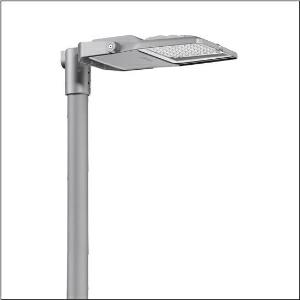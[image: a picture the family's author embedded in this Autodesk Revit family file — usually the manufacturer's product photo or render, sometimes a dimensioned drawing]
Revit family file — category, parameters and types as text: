
# Revit family: floodlight_fl_21_mini___pl33t_5xa7775c2f3a_8bfe
name_source: partatom
category: Lighting Fixtures
units: mm (PartAtom-declared; Revit-internal decimal feet)

## family parameters
Cut with Voids When Loaded = No
Host = Face
Light Source = No
Part Type = Normal
Room Calculation Point = No
Round Connector Dimension = Use Diameter
Shared = No

## types (1)
- --- (1 x LED, 12050 lm, 89 W, 3000K)
    Apparent Load = 89 VA
    CIE Flux Codes = 26 75 99 100 100
    Color Rendering = 70
    Color Temperature = 3000K
    Default Elevation = 1800 mm
    Description = Floodlight FL 21 mini, floodlight, primary light control with lens, of PMMA, primary optical cover: protective disc, of toughened safety glass, transparent, light distribution: PL33T, light emission: direct distribution, installation type: surface-mounted, LED, High Power LED, rated luminous flux: 12.050lm, luminous efficacy: 135lm/W, light colour: 730, colour temperature: 3000K, control: flexible luminous flux parameterisation, time-dependent luminous flux control, constant luminous flux control, overheat protection, presetting dimming logarithmic, with terminal, 6-pole, mains connection: 220..240V, AC, 50/60Hz, start of lifetime: 89W, end of service life: 94W, reduction: 43W, luminaire housing, of diecast aluminium, powder-coated, Siteco® metallic grey (DB 702S), corrosivity category C5 mid according to DIN EN ISO 12944, sealing non-destructively replaceable, please order mast flange separately, mast bracket, of steel, galvanised, powder-coated, Siteco® metallic grey (DB 702S), Smart Interface above, protection rating (complete): IP66, insulation class (complete): insulation class II (safety insulation), certification: CE, ENEC, VDE, protection symbol: D, impact resistance: IK08, permissible operating ambient temperature: -40..+40°C, permissible operating ambient temperature for outdoor applications: -40..+50°C, standard: DIN EN 12944, LABS conformity tested according to VDMA 24364:2018-05, packaging unit: 1 piece

Light Distribution: PL33T
    Height = 70 mm
    Lamp = 1 x LED
    Lamp Light Flux = 12050 lm
    Lamp Power = 89 W
    Lamp count = 1
    Length = 485 mm
    Luminous efficacy = 135 lm/W
    Manufacturer = Siteco
    ModVariant = No
    Model = 5XA7775C2F3A
    Number of Poles = 1
    OnlyDefault = Yes
    Power Factor = 1
    Product Name = Floodlight FL 21 mini | PL33T
    Product group = floodlight | pylon annexe
    ProductGroupID = 6200
    Protection Class = Protection class II
    Protection Degree = IP 66
    RLX_Detail_Level = 1
    RLX_Emergency_Light_Flux = 0 lm
    RLX_Emergency_Type = 0
    RLX_Emergency_Type_DB = No
    RlxData = <blob elided: 100777 chars, md5=d8473b74>
    Socket = socket
    Standby Power = 0 W
    System Light Flux = 12050 lm
    System Power = 89 W
    Type Comments = factory setting: luminous flux: 100 % | dim-lin: 254 | 456 mA
    Type Image = l_1007125.jpg
    URL = http://relux.com
    VarID = @adj_081025
    Voltage = 0 V
    Weight = 0.00 kg
    Width = 337 mm

## geometry (parser evidence)
native form markers: Blend x4, Sweep x10
no freeform markers — native parametric forms only
